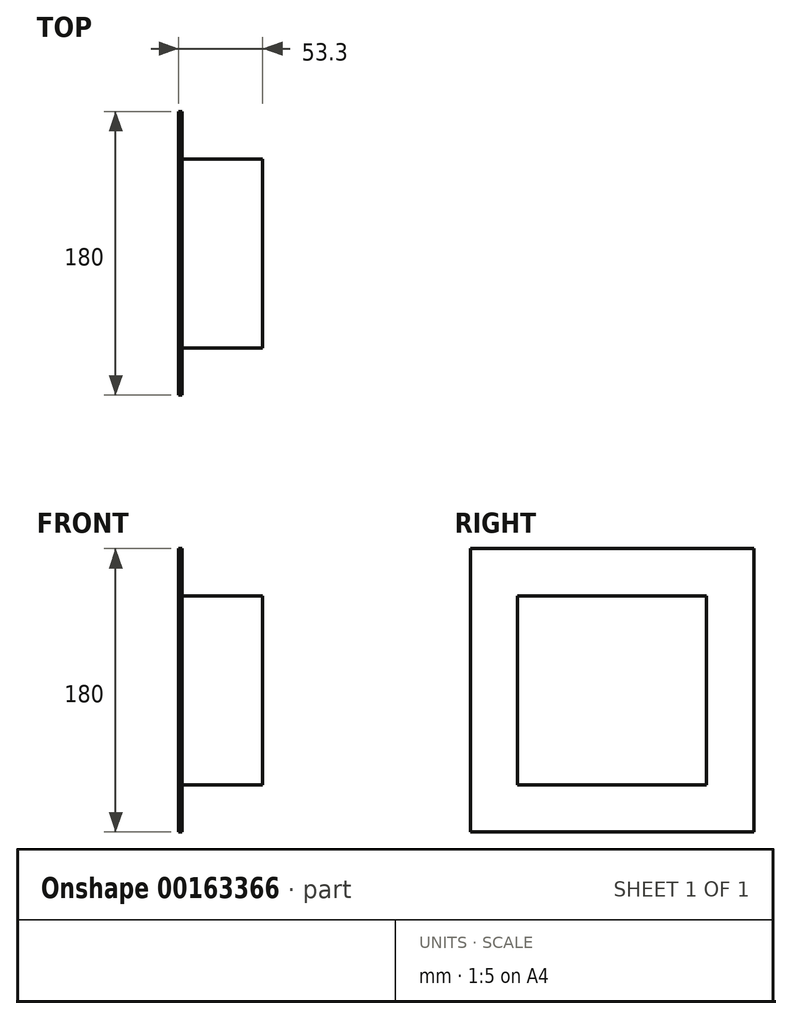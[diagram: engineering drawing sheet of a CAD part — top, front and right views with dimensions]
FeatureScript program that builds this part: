
annotation { "Feature Type Name" : "Feature", "Feature Type Description" : "" }
export const myFeature = defineFeature(function(context is Context, id is Id, definition is map)
    precondition{}
    {
        {
            var Q0;
            Q0=qCreatedBy(makeId("Right.planeOp"),FACE);
            var sketch = newSketch(context, id + "F0", { "sketchPlane" : qUnion([Q0])});
            skLineSegment(sketch, "E0.bottom", {"start": v(90, -90) * mm, "end": v(-90, -90) * mm});
            skLineSegment(sketch, "E0.top", {"start": v(90, 90) * mm, "end": v(-90, 90) * mm});
            skLineSegment(sketch, "E0.left", {"start": v(90, -90) * mm, "end": v(90, 90) * mm});
            skLineSegment(sketch, "E0.right", {"start": v(-90, -90) * mm, "end": v(-90, 90) * mm});
            skPoint(sketch, "E0.middle", {"position": v(0, 0) * mm});
            skSolve(sketch);
        }
        {
            var Q0;
            Q0 = qSketchRegion(id + "F0", true);
            extrude(context, id + "F1", {"entities" : qUnion([Q0]), "depth" : 2.3 * mm});
        }
        {
            var Q0;
            Q0=makeQuery(id+"F1.opExtrude","CAP_FACE",FACE,{"disambiguationData":[OSD([sQuery(id+"F0.wireOp",EDGE,"E0.bottom"),sQuery(id+"F0.wireOp",EDGE,"E0.top"),sQuery(id+"F0.wireOp",EDGE,"E0.left"),sQuery(id+"F0.wireOp",EDGE,"E0.right")])],"isStart":false});
            var sketch = newSketch(context, id + "F2", { "sketchPlane" : qUnion([Q0])});
            skLineSegment(sketch, "E1.bottom", {"start": v(60, -60) * mm, "end": v(-60, -60) * mm});
            skLineSegment(sketch, "E1.top", {"start": v(60, 60) * mm, "end": v(-60, 60) * mm});
            skLineSegment(sketch, "E1.left", {"start": v(60, -60) * mm, "end": v(60, 60) * mm});
            skLineSegment(sketch, "E1.right", {"start": v(-60, -60) * mm, "end": v(-60, 60) * mm});
            skPoint(sketch, "E1.middle", {"position": v(0, 0) * mm});
            skSolve(sketch);
        }
        {
            var Q0;
            Q0 = qSketchRegion(id + "F2", true);
            extrude(context, id + "F3", {"entities" : qUnion([Q0]), "operationType" : NewBodyOperationType.ADD, "depth" : 51 * mm});
        }
    });
